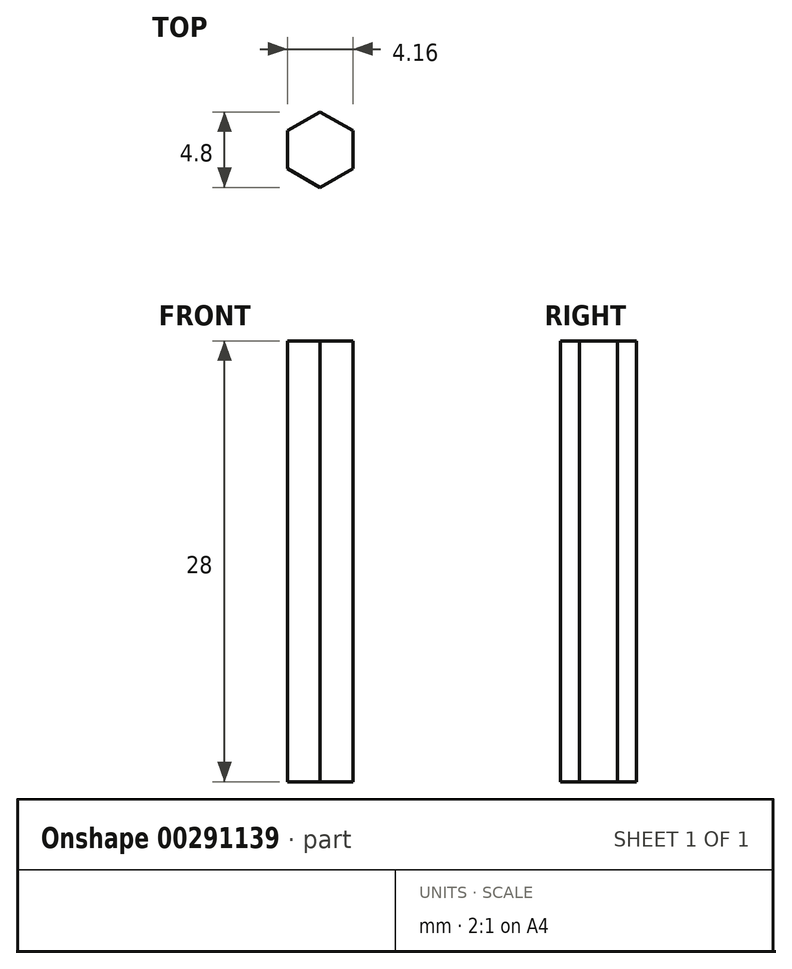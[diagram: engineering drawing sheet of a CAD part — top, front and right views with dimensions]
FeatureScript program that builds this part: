
annotation { "Feature Type Name" : "Feature", "Feature Type Description" : "" }
export const myFeature = defineFeature(function(context is Context, id is Id, definition is map)
    precondition{}
    {
        {
            var Q0;
            Q0=qCreatedBy(makeId("Top.planeOp"),FACE);
            var sketch = newSketch(context, id + "F0", { "sketchPlane" : qUnion([Q0])});
            skLineSegment(sketch, "E0", {"start": v(0, 4.8) * mm, "end": v(-2.08, 3.6) * mm});
            skLineSegment(sketch, "E1", {"start": v(-2.08, 3.6) * mm, "end": v(-2.08, 1.2) * mm});
            skLineSegment(sketch, "E2", {"start": v(-2.08, 1.2) * mm, "end": v(0, 0) * mm});
            skLineSegment(sketch, "E3", {"start": v(0, 0) * mm, "end": v(2.08, 1.2) * mm});
            skLineSegment(sketch, "E4", {"start": v(2.08, 1.2) * mm, "end": v(2.08, 3.6) * mm});
            skLineSegment(sketch, "E5", {"start": v(2.08, 3.6) * mm, "end": v(0, 4.8) * mm});
            skPoint(sketch, "E6", {"position": v(0, 2.4) * mm});
            skLineSegment(sketch, "E7", {"start": v(0, 4.8) * mm, "end": v(0, 2.4) * mm, "construction": true});
            skLineSegment(sketch, "E8", {"start": v(0, 0) * mm, "end": v(0, 2.4) * mm, "construction": true});
            skSolve(sketch);
        }
        {
            var Q0;
            Q0 = qSketchRegion(id + "F0", true);
            extrude(context, id + "F1", {"entities" : qUnion([Q0]), "depth" : 28 * mm});
        }
    });
